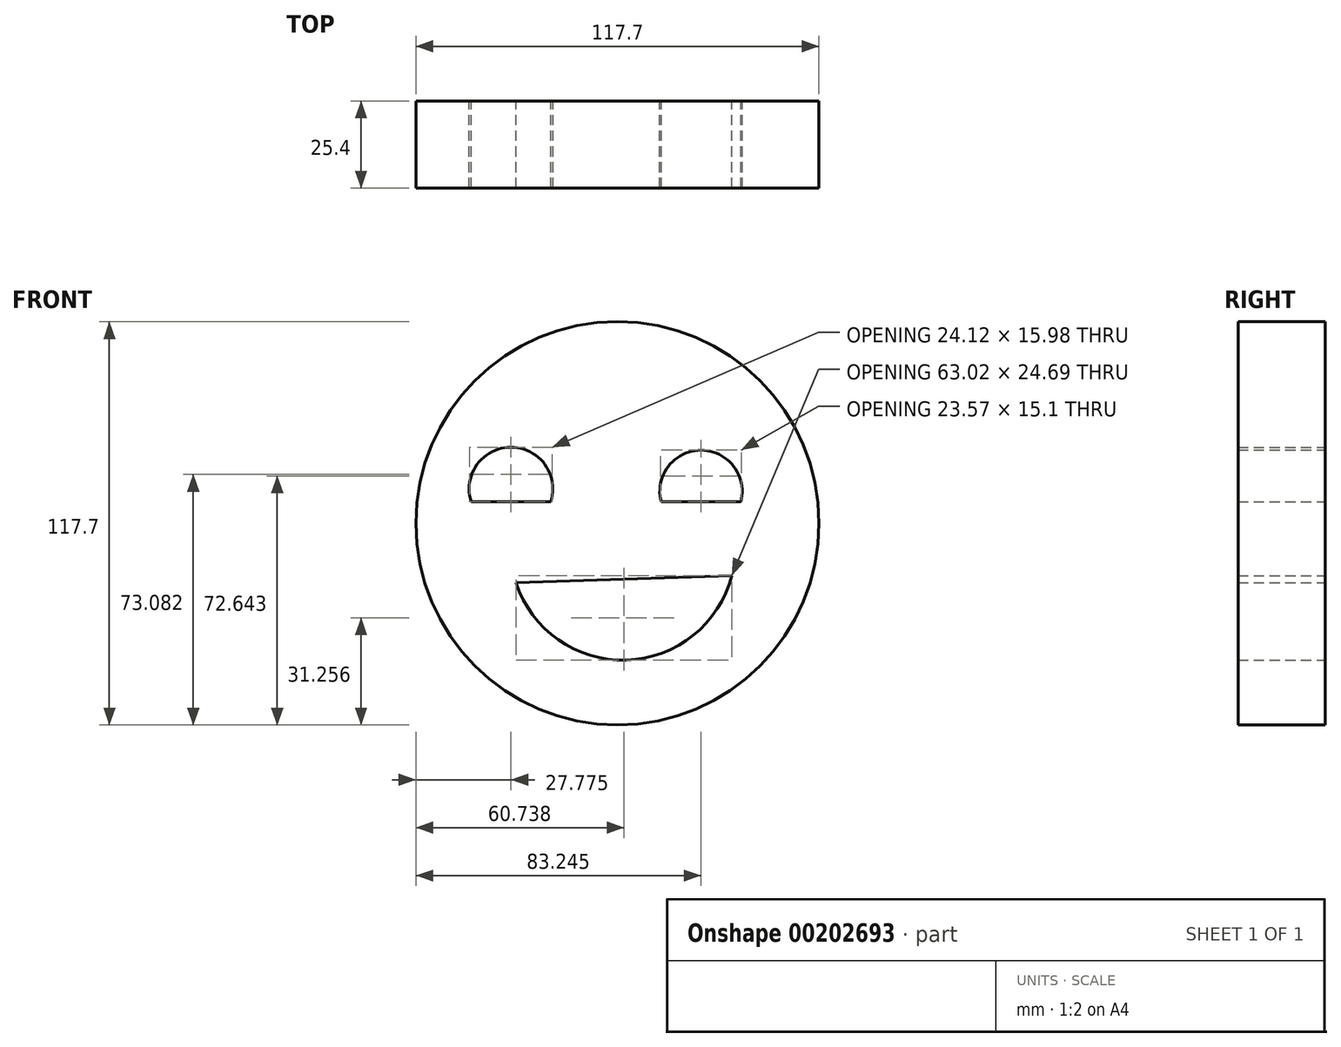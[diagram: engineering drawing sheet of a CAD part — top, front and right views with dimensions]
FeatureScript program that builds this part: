
annotation { "Feature Type Name" : "Feature", "Feature Type Description" : "" }
export const myFeature = defineFeature(function(context is Context, id is Id, definition is map)
    precondition{}
    {
        {
            var Q0;
            Q0=qCreatedBy(makeId("Front.planeOp"),FACE);
            var sketch = newSketch(context, id + "F0", { "sketchPlane" : qUnion([Q0])});
            skCircle(sketch, "E0", {"center": v(0, 0) * mm, "radius": 58.85 * mm});
            skLineSegment(sketch, "E1", {"start": v(-42.7, 6.24) * mm, "end": v(-19.46, 6.24) * mm});
            skLineSegment(sketch, "E2", {"start": v(36.01, 6.24) * mm, "end": v(12.78, 6.24) * mm});
            skArc(sketch, "E3", {"start": v(-19.46, 6.24) * mm, "mid": v(-31.07, 22.22) * mm, "end": v(-42.7, 6.24) * mm});
            skArc(sketch, "E4", {"start": v(36.01, 6.24) * mm, "mid": v(24.4, 21.34) * mm, "end": v(12.78, 6.24) * mm});
            skArc(sketch, "E5", {"start": v(-29.62, -17.28) * mm, "mid": v(2.65, -39.94) * mm, "end": v(33.4, -15.25) * mm});
            skLineSegment(sketch, "E6", {"start": v(-29.62, -17.28) * mm, "end": v(33.4, -15.25) * mm});
            skArc(sketch, "E7", {"start": v(19.84, -34.42) * mm, "mid": v(6.2, -28.58) * mm, "end": v(-3.85, -39.5) * mm});
            skSolve(sketch);
        }
        {
            var Q0;
            Q0=makeQuery(id+"F0.imprint","IMPRINT",FACE,{"disambiguationData":[TD([[makeQuery(id+"F0.imprint","IMPRINT",EDGE,{"derivedFrom":sQuery(id+"F0.wireOp",EDGE,"E0")}),1.0]])]});
            extrude(context, id + "F1", {"entities" : qUnion([Q0]), "depth" : 25.4 * mm});
        }
    });
